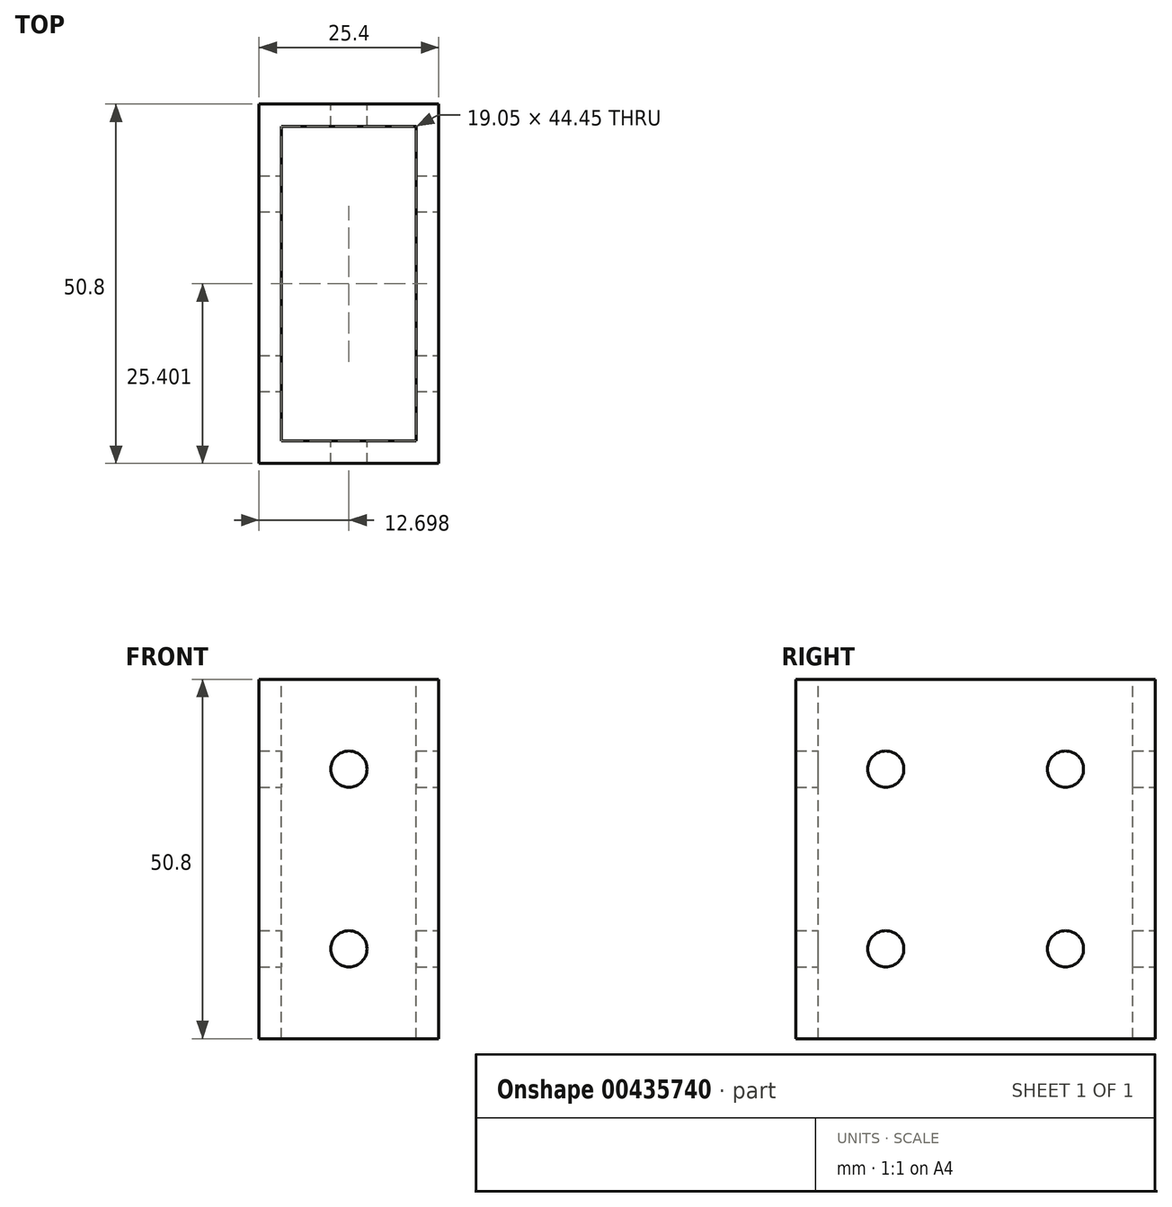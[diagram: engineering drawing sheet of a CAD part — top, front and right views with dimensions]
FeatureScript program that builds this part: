
annotation { "Feature Type Name" : "Feature", "Feature Type Description" : "" }
export const myFeature = defineFeature(function(context is Context, id is Id, definition is map)
    precondition{}
    {
        {
            var Q0;
            Q0=qCreatedBy(makeId("Top.planeOp"),FACE);
            var sketch = newSketch(context, id + "F0", { "sketchPlane" : qUnion([Q0])});
            skLineSegment(sketch, "E0.bottom", {"start": v(-12.07, 35.12) * mm, "end": v(13.33, 35.12) * mm});
            skLineSegment(sketch, "E0.top", {"start": v(-12.07, -15.68) * mm, "end": v(13.33, -15.68) * mm});
            skLineSegment(sketch, "E0.left", {"start": v(-12.07, 35.12) * mm, "end": v(-12.07, -15.68) * mm});
            skLineSegment(sketch, "E0.right", {"start": v(13.33, 35.12) * mm, "end": v(13.33, -15.68) * mm});
            skSolve(sketch);
        }
        {
            var Q0;
            Q0=makeQuery(id+"F0.imprint","IMPRINT",FACE,{"disambiguationData":[TD([[makeQuery(id+"F0.imprint","IMPRINT",EDGE,{"derivedFrom":sQuery(id+"F0.wireOp",EDGE,"E0.bottom")}),-1.0]])]});
            extrude(context, id + "F1", {"entities" : qUnion([Q0]), "depth" : 50.8 * mm});
        }
        {
            var Q0;
            Q0=makeQuery(id+"F1.opExtrude","CAP_FACE",FACE,{"disambiguationData":[OSD([sQuery(id+"F0.wireOp",EDGE,"E0.bottom"),sQuery(id+"F0.wireOp",EDGE,"E0.top"),sQuery(id+"F0.wireOp",EDGE,"E0.left"),sQuery(id+"F0.wireOp",EDGE,"E0.right")])],"isStart":false});
            var sketch = newSketch(context, id + "F2", { "sketchPlane" : qUnion([Q0])});
            skLineSegment(sketch, "E1.bottom", {"start": v(-8.9, 31.95) * mm, "end": v(10.15, 31.95) * mm});
            skLineSegment(sketch, "E1.top", {"start": v(-8.9, -12.5) * mm, "end": v(10.15, -12.5) * mm});
            skLineSegment(sketch, "E1.left", {"start": v(-8.9, 31.95) * mm, "end": v(-8.9, -12.5) * mm});
            skLineSegment(sketch, "E1.right", {"start": v(10.15, 31.95) * mm, "end": v(10.15, -12.5) * mm});
            skSolve(sketch);
        }
        {
            var Q0;
            Q0=makeQuery(id+"F2.imprint","IMPRINT",FACE,{"disambiguationData":[TD([[makeQuery(id+"F2.imprint","IMPRINT",EDGE,{"derivedFrom":sQuery(id+"F2.wireOp",EDGE,"E1.bottom")}),-1.0]])]});
            extrude(context, id + "F3", {"entities" : qUnion([Q0]), "operationType" : NewBodyOperationType.REMOVE, "oppositeDirection" : true, "depth" : 50.8 * mm});
        }
        {
            var Q0;
            Q0=makeQuery(id+"F1.opExtrude","SWEPT_FACE",FACE,{"disambiguationData":[OSD([sQuery(id+"F0.wireOp",EDGE,"E0.right")])]});
            var sketch = newSketch(context, id + "F4", { "sketchPlane" : qUnion([Q0])});
            skCircle(sketch, "E2", {"center": v(-2.98, 38.1) * mm, "radius": 2.55 * mm});
            skCircle(sketch, "E3.0.1.0", {"center": v(-2.98, 12.7) * mm, "radius": 2.55 * mm});
            skCircle(sketch, "E3.1.0.0", {"center": v(22.42, 38.1) * mm, "radius": 2.55 * mm});
            skCircle(sketch, "E3.1.1.0", {"center": v(22.42, 12.7) * mm, "radius": 2.55 * mm});
            skLineSegment(sketch, "E3.direction1", {"start": v(-2.98, 38.1) * mm, "end": v(22.42, 38.1) * mm, "construction": true});
            skLineSegment(sketch, "E3.direction2", {"start": v(-2.98, 38.1) * mm, "end": v(-2.98, 12.7) * mm, "construction": true});
            skSolve(sketch);
        }
        {
            var Q0;
            Q0=sQuery(id+"F4.wireOp",VERTEX,"E2.center");
            var Q1;
            Q1=sQuery(id+"F4.wireOp",VERTEX,"E3.0.1.0.center");
            var Q2;
            Q2=sQuery(id+"F4.wireOp",VERTEX,"E3.1.0.0.center");
            var Q3;
            Q3=sQuery(id+"F4.wireOp",VERTEX,"E3.1.1.0.center");
            var Q4;
            Q4=makeQuery(id+"F1.opExtrude","SWEPT_BODY",BODY,{"disambiguationData":[OSD([sQuery(id+"F0.wireOp",EDGE,"E0.bottom"),sQuery(id+"F0.wireOp",EDGE,"E0.top"),sQuery(id+"F0.wireOp",EDGE,"E0.left"),sQuery(id+"F0.wireOp",EDGE,"E0.right")])]});
            hole(context, id + "F5", {"style" : HoleStyle.SIMPLE, "endStyle" : HoleEndStyle.THROUGH, "holeDiameter" : 5.1 * mm, "isTappedThrough" : true, "tappedDepth" : 12.7 * mm, "tapClearance" : 3, "locations" : qUnion([Q0, Q1, Q2, Q3]), "scope" : qUnion([Q4])});
        }
        {
            var Q0;
            Q0=makeQuery(id+"F1.opExtrude","SWEPT_FACE",FACE,{"disambiguationData":[OSD([sQuery(id+"F0.wireOp",EDGE,"E0.bottom")])]});
            var sketch = newSketch(context, id + "F6", { "sketchPlane" : qUnion([Q0])});
            skCircle(sketch, "E4", {"center": v(-0.63, 38.1) * mm, "radius": 2.55 * mm});
            skCircle(sketch, "E5.0.1.0", {"center": v(-0.63, 12.7) * mm, "radius": 2.55 * mm});
            skLineSegment(sketch, "E5.direction1", {"start": v(-0.63, 38.1) * mm, "end": v(24.77, 38.1) * mm, "construction": true});
            skLineSegment(sketch, "E5.direction2", {"start": v(-0.63, 38.1) * mm, "end": v(-0.63, 12.7) * mm, "construction": true});
            skSolve(sketch);
        }
        {
            var Q0;
            Q0=sQuery(id+"F6.wireOp",VERTEX,"E4.center");
            var Q1;
            Q1=sQuery(id+"F6.wireOp",VERTEX,"E5.0.1.0.center");
            var Q2;
            Q2=makeQuery(id+"F1.opExtrude","SWEPT_BODY",BODY,{"disambiguationData":[OSD([sQuery(id+"F0.wireOp",EDGE,"E0.bottom"),sQuery(id+"F0.wireOp",EDGE,"E0.top"),sQuery(id+"F0.wireOp",EDGE,"E0.left"),sQuery(id+"F0.wireOp",EDGE,"E0.right")])]});
            hole(context, id + "F7", {"style" : HoleStyle.SIMPLE, "endStyle" : HoleEndStyle.THROUGH, "holeDiameter" : 5.1 * mm, "isTappedThrough" : true, "tappedDepth" : 12.7 * mm, "tapClearance" : 3, "locations" : qUnion([Q0, Q1]), "scope" : qUnion([Q2])});
        }
    });
